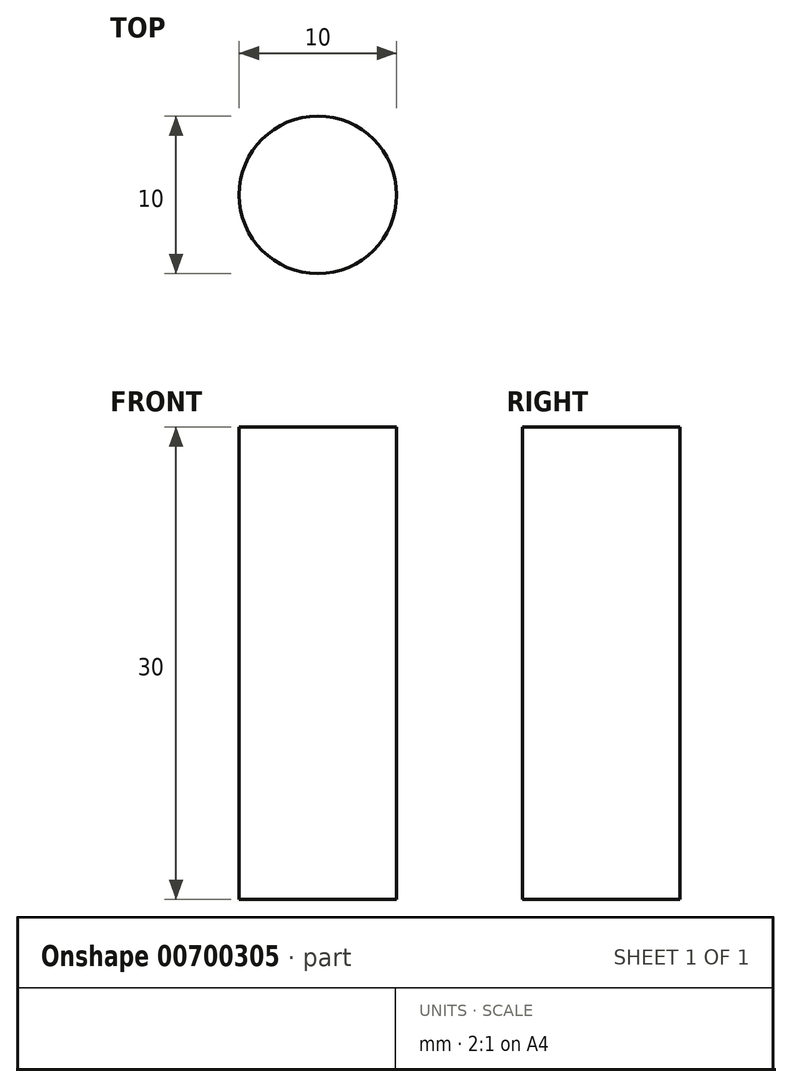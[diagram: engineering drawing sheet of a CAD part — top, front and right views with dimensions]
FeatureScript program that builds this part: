
annotation { "Feature Type Name" : "Feature", "Feature Type Description" : "" }
export const myFeature = defineFeature(function(context is Context, id is Id, definition is map)
    precondition{}
    {
        {
            var Q0;
            Q0=qCreatedBy(makeId("Top.planeOp"),FACE);
            var sketch = newSketch(context, id + "F0", { "sketchPlane" : qUnion([Q0])});
            skCircle(sketch, "E0", {"center": v(0, 0) * mm, "radius": 5 * mm});
            skSolve(sketch);
        }
        {
            var Q0;
            Q0 = qSketchRegion(id + "F0", true);
            extrude(context, id + "F1", {"entities" : qUnion([Q0]), "depth" : 30 * mm, "offsetDistance" : 25 * mm});
        }
    });
